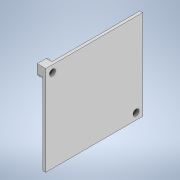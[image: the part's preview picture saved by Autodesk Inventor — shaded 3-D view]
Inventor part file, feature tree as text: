
AUTODESK INVENTOR PART (.ipt)
format: ipt  version: 2021 (Build 250183000, 183)  size: 140,800 bytes
history: native  units: mm
features: extrude x4, sketch x3, pattern_circular x1, projected_geometry x1
ambient origin geometry x8: Origin, YZ Plane, XZ Plane, XY Plane, X Axis, Y Axis, Z Axis, Center Point
bodies: Solid1 (feature_tree)
feature tree (9):
  extrude  "Extrusion1"  Depth=64.0mm
  sketch  "Sketch2"  dims[d2=2.0mm d3=0.0mm d4=7.5mm]
  extrude  "Extrusion2"  Depth=2.0mm
  extrude  "Extrusion3"  Depth=5.0mm
  pattern_circular  "Circular Pattern1"  [2 undecoded]
  extrude  "Extrusion4"  Depth=4.0mm TaperAngle=0.0deg
  sketch  "Sketch1"  dims[d0=69.0mm d1=64.0mm]
  sketch  "Sketch3"  dims[d5=10.0mm d6=5.0mm d7=5.0mm d8=4.0mm d9=0.0mm d10=4.3mm d11=4.0mm d12=0.0mm d13=20.0mm d14=360.0deg d16=0.25mm d17=0.25mm d18=0.0mm d19=0.0mm]
  projected_geometry  "Projected Loop1"
note: 2 required parameter values undecoded (feature->parameter linkage not recoverable at this tier; creation-order binding heuristic only, values carry confidence <= 0.55)
